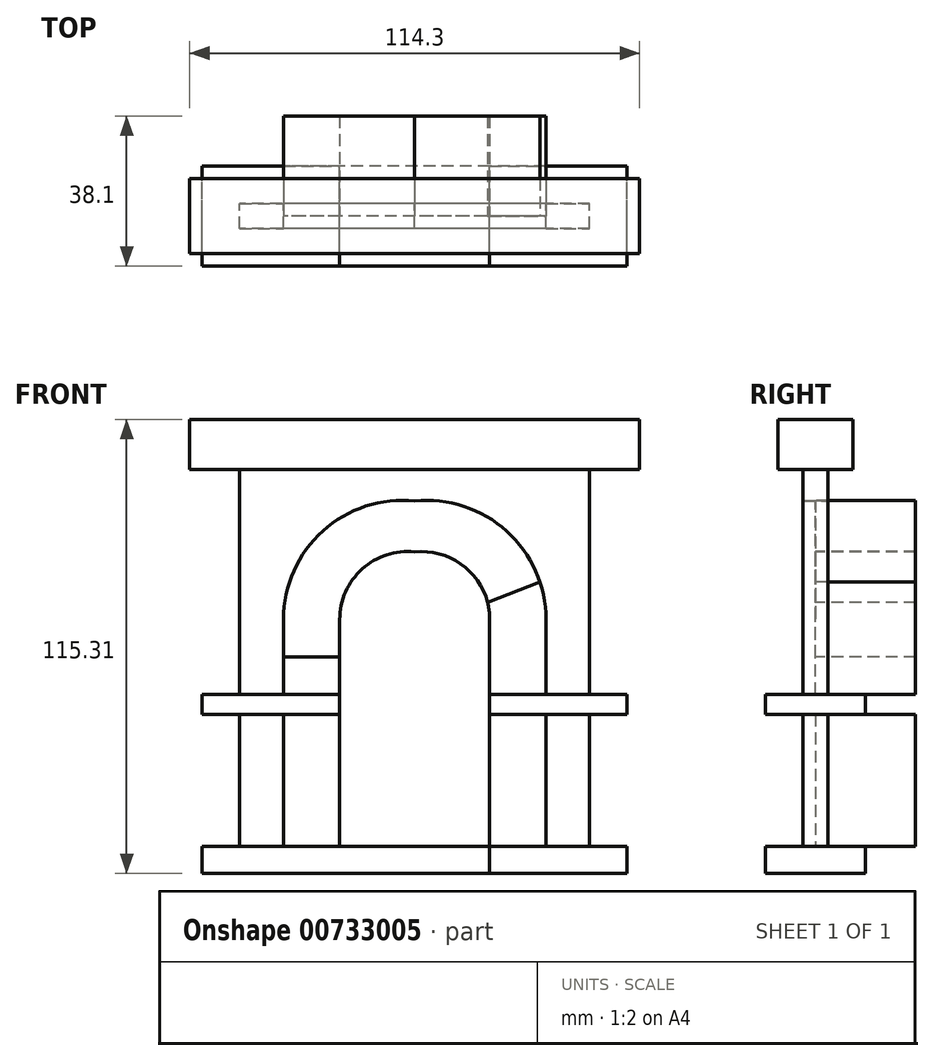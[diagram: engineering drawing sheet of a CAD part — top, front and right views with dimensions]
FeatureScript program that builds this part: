
annotation { "Feature Type Name" : "Feature", "Feature Type Description" : "" }
export const myFeature = defineFeature(function(context is Context, id is Id, definition is map)
    precondition{}
    {
        {
            var Q0;
            Q0=qCreatedBy(makeId("Front.planeOp"),FACE);
            var sketch = newSketch(context, id + "F0", { "sketchPlane" : qUnion([Q0])});
            skLineSegment(sketch, "E0", {"start": v(-44.45, 0) * mm, "end": v(-19.05, 0) * mm});
            skLineSegment(sketch, "E1", {"start": v(-19.05, 0) * mm, "end": v(-19.05, 19.05) * mm});
            skLineSegment(sketch, "E2", {"start": v(44.45, 0) * mm, "end": v(44.45, 57.15) * mm});
            skLineSegment(sketch, "E3", {"start": v(44.45, 0) * mm, "end": v(19.05, 0) * mm});
            skLineSegment(sketch, "E4", {"start": v(19.05, 0) * mm, "end": v(19.05, 19.05) * mm});
            skArc(sketch, "E5", {"start": v(-19.05, 19.05) * mm, "mid": v(-13.34, 31.87) * mm, "end": v(0, 36.22) * mm});
            skArc(sketch, "E6", {"start": v(19.05, 19.05) * mm, "mid": v(13.34, 31.87) * mm, "end": v(0, 36.22) * mm});
            skLineSegment(sketch, "E7", {"start": v(33.33, 0) * mm, "end": v(33.33, 19.05) * mm});
            skLineSegment(sketch, "E8", {"start": v(-33.33, 0) * mm, "end": v(-33.33, 19.15) * mm});
            skLineSegment(sketch, "E9", {"start": v(-44.45, 0) * mm, "end": v(-44.45, 57.15) * mm});
            skArc(sketch, "E10", {"start": v(-33.33, 19.15) * mm, "mid": v(-23.34, 41.56) * mm, "end": v(0, 49.13) * mm});
            skArc(sketch, "E11", {"start": v(33.33, 19.05) * mm, "mid": v(23.35, 41.5) * mm, "end": v(0, 49.13) * mm});
            skLineSegment(sketch, "E12", {"start": v(19.05, 0) * mm, "end": v(19.05, -5.1) * mm});
            skLineSegment(sketch, "E13", {"start": v(-19.05, 0) * mm, "end": v(-19.05, -5.1) * mm});
            skLineSegment(sketch, "E14", {"start": v(19.05, -5.1) * mm, "end": v(53.98, -5.1) * mm});
            skLineSegment(sketch, "E15", {"start": v(53.98, -5.1) * mm, "end": v(53.98, 0) * mm});
            skLineSegment(sketch, "E16", {"start": v(53.98, 0) * mm, "end": v(44.45, 0) * mm});
            skLineSegment(sketch, "E17", {"start": v(44.45, 57.15) * mm, "end": v(57.15, 57.15) * mm});
            skLineSegment(sketch, "E18", {"start": v(57.15, 57.15) * mm, "end": v(57.15, 69.85) * mm});
            skLineSegment(sketch, "E19", {"start": v(57.15, 69.85) * mm, "end": v(-57.15, 69.85) * mm});
            skLineSegment(sketch, "E20", {"start": v(-57.15, 69.85) * mm, "end": v(-57.15, 57.15) * mm});
            skLineSegment(sketch, "E21", {"start": v(-57.15, 57.15) * mm, "end": v(-44.45, 57.15) * mm});
            skLineSegment(sketch, "E22", {"start": v(44.45, 57.15) * mm, "end": v(-44.45, 57.15) * mm});
            skLineSegment(sketch, "E23", {"start": v(44.45, -5.1) * mm, "end": v(44.45, -38.63) * mm});
            skLineSegment(sketch, "E24", {"start": v(-44.45, -5.1) * mm, "end": v(-44.45, -38.63) * mm});
            skLineSegment(sketch, "E25", {"start": v(-19.05, -5.1) * mm, "end": v(-19.05, -38.63) * mm});
            skLineSegment(sketch, "E26", {"start": v(19.05, -5.1) * mm, "end": v(19.05, -38.63) * mm});
            skLineSegment(sketch, "E27", {"start": v(-44.45, -38.63) * mm, "end": v(-19.05, -38.63) * mm});
            skLineSegment(sketch, "E28", {"start": v(19.05, -38.63) * mm, "end": v(44.45, -38.63) * mm});
            skLineSegment(sketch, "E29", {"start": v(33.33, -5.1) * mm, "end": v(33.33, -38.63) * mm});
            skLineSegment(sketch, "E30", {"start": v(-33.33, -5.1) * mm, "end": v(-33.33, -38.63) * mm});
            skLineSegment(sketch, "E31", {"start": v(-19.05, -5.1) * mm, "end": v(-33.33, -5.1) * mm});
            skLineSegment(sketch, "E32", {"start": v(-33.33, -5.1) * mm, "end": v(-44.45, -5.1) * mm});
            skLineSegment(sketch, "E33", {"start": v(-44.45, -5.1) * mm, "end": v(-53.98, -5.1) * mm});
            skLineSegment(sketch, "E34", {"start": v(-53.98, -5.1) * mm, "end": v(-53.98, 0) * mm});
            skLineSegment(sketch, "E35", {"start": v(-53.98, 0) * mm, "end": v(-44.45, 0) * mm});
            skLineSegment(sketch, "E36", {"start": v(-19.05, 9.53) * mm, "end": v(-33.33, 9.53) * mm});
            skLineSegment(sketch, "E37", {"start": v(0, 49.13) * mm, "end": v(0, 36.22) * mm});
            skLineSegment(sketch, "E38", {"start": v(12.2, 32.81) * mm, "end": v(19, 44.77) * mm});
            skLineSegment(sketch, "E39", {"start": v(-12.2, 32.81) * mm, "end": v(-19.07, 44.77) * mm});
            skLineSegment(sketch, "E40", {"start": v(18.5, 23.34) * mm, "end": v(31.79, 28.59) * mm});
            skLineSegment(sketch, "E41", {"start": v(-18.5, 23.34) * mm, "end": v(-31.81, 28.59) * mm});
            skLineSegment(sketch, "E42", {"start": v(-33.33, -21.86) * mm, "end": v(-19.05, -21.86) * mm});
            skLineSegment(sketch, "E43", {"start": v(19.05, -21.86) * mm, "end": v(33.33, -21.86) * mm});
            skLineSegment(sketch, "E44", {"start": v(44.45, -38.63) * mm, "end": v(53.98, -38.63) * mm});
            skLineSegment(sketch, "E45", {"start": v(-44.45, -38.63) * mm, "end": v(-53.98, -38.63) * mm});
            skLineSegment(sketch, "E46", {"start": v(53.98, -38.63) * mm, "end": v(53.98, -45.46) * mm});
            skLineSegment(sketch, "E47", {"start": v(-53.98, -38.63) * mm, "end": v(-53.98, -45.46) * mm});
            skLineSegment(sketch, "E48", {"start": v(53.98, -45.46) * mm, "end": v(-53.98, -45.46) * mm});
            skLineSegment(sketch, "E49", {"start": v(19.05, -38.63) * mm, "end": v(-19.05, -38.63) * mm});
            skLineSegment(sketch, "E50", {"start": v(-19.05, -38.63) * mm, "end": v(-19.05, -45.46) * mm});
            skLineSegment(sketch, "E51", {"start": v(19.05, -38.63) * mm, "end": v(19.05, -45.46) * mm});
            skLineSegment(sketch, "E52", {"start": v(19.05, 9.52) * mm, "end": v(33.33, 9.53) * mm});
            skLineSegment(sketch, "E53", {"start": v(-44.45, 57.15) * mm, "end": v(44.45, 57.15) * mm});
            skSolve(sketch);
        }
        {
            var Q0;
            Q0=makeQuery(id+"F0.imprint","IMPRINT",FACE,{"disambiguationData":[TD([[makeQuery(id+"F0.imprint","IMPRINT",EDGE,{"derivedFrom":sQuery(id+"F0.wireOp",EDGE,"E17")}),1.0]])]});
            extrude(context, id + "F1", {"entities" : qUnion([Q0]), "endBound" : BoundingType.SYMMETRIC, "depth" : 19.05 * mm, "offsetDistance" : 25.4 * mm});
        }
        {
            var Q0;
            {var subQ3=sQuery(id+"F0.wireOp",EDGE,"E1");Q0=makeQuery(id+"F0.imprint","IMPRINT",FACE,{"disambiguationData":[TD([[makeQuery(id+"F0.imprint","IMPRINT",EDGE,{"derivedFrom":subQ3}),1.0]])]});}
            var Q1;
            {var subQ0=sQuery(id+"F0.wireOp",EDGE,"E26");Q1=makeQuery(id+"F0.imprint","IMPRINT",FACE,{"disambiguationData":[TD([[makeQuery(id+"F0.imprint","IMPRINT",EDGE,{"derivedFrom":subQ0}),1.0]])]});}
            var Q2;
            {var subQ0=sQuery(id+"F0.wireOp",EDGE,"E25");Q2=makeQuery(id+"F0.imprint","IMPRINT",FACE,{"disambiguationData":[TD([[makeQuery(id+"F0.imprint","IMPRINT",EDGE,{"derivedFrom":subQ0}),-1.0]])]});}
            extrude(context, id + "F2", {"entities" : qUnion([Q0, Q1, Q2]), "oppositeDirection" : true, "depth" : 25.4 * mm, "offsetDistance" : 25.4 * mm});
        }
        {
            var Q0;
            {var subQ1=sQuery(id+"F0.wireOp",EDGE,"E12");Q0=makeQuery(id+"F0.imprint","IMPRINT",FACE,{"disambiguationData":[TD([[makeQuery(id+"F0.imprint","IMPRINT",EDGE,{"derivedFrom":subQ1}),1.0]])]});}
            var Q1;
            {var subQ0=sQuery(id+"F0.wireOp",EDGE,"E13");Q1=makeQuery(id+"F0.imprint","IMPRINT",FACE,{"disambiguationData":[TD([[makeQuery(id+"F0.imprint","IMPRINT",EDGE,{"derivedFrom":subQ0}),-1.0]])]});}
            extrude(context, id + "F3", {"entities" : qUnion([Q0, Q1]), "endBound" : BoundingType.SYMMETRIC, "depth" : 25.4 * mm, "offsetDistance" : 25.4 * mm});
        }
        {
            var Q0;
            {var subQ0=sQuery(id+"F0.wireOp",EDGE,"E23");Q0=makeQuery(id+"F0.imprint","IMPRINT",FACE,{"disambiguationData":[TD([[makeQuery(id+"F0.imprint","IMPRINT",EDGE,{"derivedFrom":subQ0}),-1.0]])]});}
            var Q1;
            {var subQ2=sQuery(id+"F0.wireOp",EDGE,"E2");Q1=makeQuery(id+"F0.imprint","IMPRINT",FACE,{"disambiguationData":[TD([[makeQuery(id+"F0.imprint","IMPRINT",EDGE,{"derivedFrom":subQ2}),1.0]])]});}
            var Q2;
            {var subQ0=sQuery(id+"F0.wireOp",EDGE,"E24");Q2=makeQuery(id+"F0.imprint","IMPRINT",FACE,{"disambiguationData":[TD([[makeQuery(id+"F0.imprint","IMPRINT",EDGE,{"derivedFrom":subQ0}),1.0]])]});}
            extrude(context, id + "F4", {"entities" : qUnion([Q0, Q1, Q2]), "endBound" : BoundingType.SYMMETRIC, "depth" : 6.35 * mm, "offsetDistance" : 25.4 * mm});
        }
        {
            var Q0;
            {var subQ7=sQuery(id+"F0.wireOp",EDGE,"E36");Q0=makeQuery(id+"F0.imprint","IMPRINT",FACE,{"disambiguationData":[TD([[makeQuery(id+"F0.imprint","IMPRINT",EDGE,{"derivedFrom":subQ7}),-1.0]])]});}
            var Q1;
            {var subQ0=sQuery(id+"F0.wireOp",EDGE,"E39");Q1=makeQuery(id+"F0.imprint","IMPRINT",FACE,{"disambiguationData":[TD([[makeQuery(id+"F0.imprint","IMPRINT",EDGE,{"derivedFrom":subQ0}),1.0]])]});}
            var Q2;
            {var subQ0=sQuery(id+"F0.wireOp",EDGE,"E37");Q2=makeQuery(id+"F0.imprint","IMPRINT",FACE,{"disambiguationData":[TD([[makeQuery(id+"F0.imprint","IMPRINT",EDGE,{"derivedFrom":subQ0}),-1.0]])]});}
            var Q3;
            {var subQ0=sQuery(id+"F0.wireOp",EDGE,"E37");Q3=makeQuery(id+"F0.imprint","IMPRINT",FACE,{"disambiguationData":[TD([[makeQuery(id+"F0.imprint","IMPRINT",EDGE,{"derivedFrom":subQ0}),1.0]])]});}
            var Q4;
            {var subQ0=sQuery(id+"F0.wireOp",EDGE,"E38");Q4=makeQuery(id+"F0.imprint","IMPRINT",FACE,{"disambiguationData":[TD([[makeQuery(id+"F0.imprint","IMPRINT",EDGE,{"derivedFrom":subQ0}),-1.0]])]});}
            var Q5;
            {var subQ3=sQuery(id+"F0.wireOp",EDGE,"bgtALavK-qvLX-Clxy-s0Y7-uUF01eaqvtXt");Q5=makeQuery(id+"F0.imprint","IMPRINT",FACE,{"disambiguationData":[TD([[makeQuery(id+"F0.imprint","IMPRINT",EDGE,{"derivedFrom":subQ3}),-1.0]])]});}
            var Q6;
            {var subQ5=sQuery(id+"F0.wireOp",EDGE,"bgtALavK-qvLX-Clxy-s0Y7-uUF01eaqvtXt");Q6=makeQuery(id+"F0.imprint","IMPRINT",FACE,{"disambiguationData":[TD([[makeQuery(id+"F0.imprint","IMPRINT",EDGE,{"derivedFrom":subQ5}),1.0]])]});}
            extrude(context, id + "F5", {"entities" : qUnion([Q0, Q1, Q2, Q3, Q4, Q5, Q6]), "oppositeDirection" : true, "depth" : 25.4 * mm, "offsetDistance" : 25.4 * mm});
        }
        {
            var Q0;
            {var subQ0=sQuery(id+"F0.wireOp",EDGE,"E44");Q0=makeQuery(id+"F0.imprint","IMPRINT",FACE,{"disambiguationData":[TD([[makeQuery(id+"F0.imprint","IMPRINT",EDGE,{"derivedFrom":subQ0}),-1.0]])]});}
            extrude(context, id + "F6", {"entities" : qUnion([Q0]), "endBound" : BoundingType.SYMMETRIC, "depth" : 25.4 * mm, "offsetDistance" : 25.4 * mm});
        }
        {
            var Q0;
            Q0=makeQuery(id+"F0.imprint","IMPRINT",FACE,{"disambiguationData":[TD([[makeQuery(id+"F0.imprint","IMPRINT",EDGE,{"derivedFrom":sQuery(id+"F0.wireOp",EDGE,"E49")}),1.0]])]});
            var Q1;
            {var subQ0=sQuery(id+"F0.wireOp",EDGE,"E45");Q1=makeQuery(id+"F0.imprint","IMPRINT",FACE,{"disambiguationData":[TD([[makeQuery(id+"F0.imprint","IMPRINT",EDGE,{"derivedFrom":subQ0}),1.0]])]});}
            extrude(context, id + "F7", {"entities" : qUnion([Q0, Q1]), "endBound" : BoundingType.SYMMETRIC, "depth" : 25.4 * mm, "offsetDistance" : 25.4 * mm});
        }
        {
            var Q0;
            {var subQ5=sQuery(id+"F0.wireOp",EDGE,"E52");Q0=makeQuery(id+"F0.imprint","IMPRINT",FACE,{"disambiguationData":[TD([[makeQuery(id+"F0.imprint","IMPRINT",EDGE,{"derivedFrom":subQ5}),-1.0]])]});}
            var Q1;
            {var subQ7=sQuery(id+"F0.wireOp",EDGE,"E40");Q1=makeQuery(id+"F0.imprint","IMPRINT",FACE,{"disambiguationData":[TD([[makeQuery(id+"F0.imprint","IMPRINT",EDGE,{"derivedFrom":subQ7}),-1.0]])]});}
            extrude(context, id + "F8", {"entities" : qUnion([Q0, Q1]), "oppositeDirection" : true, "depth" : 25.4 * mm, "offsetDistance" : 25.4 * mm});
        }
    });
